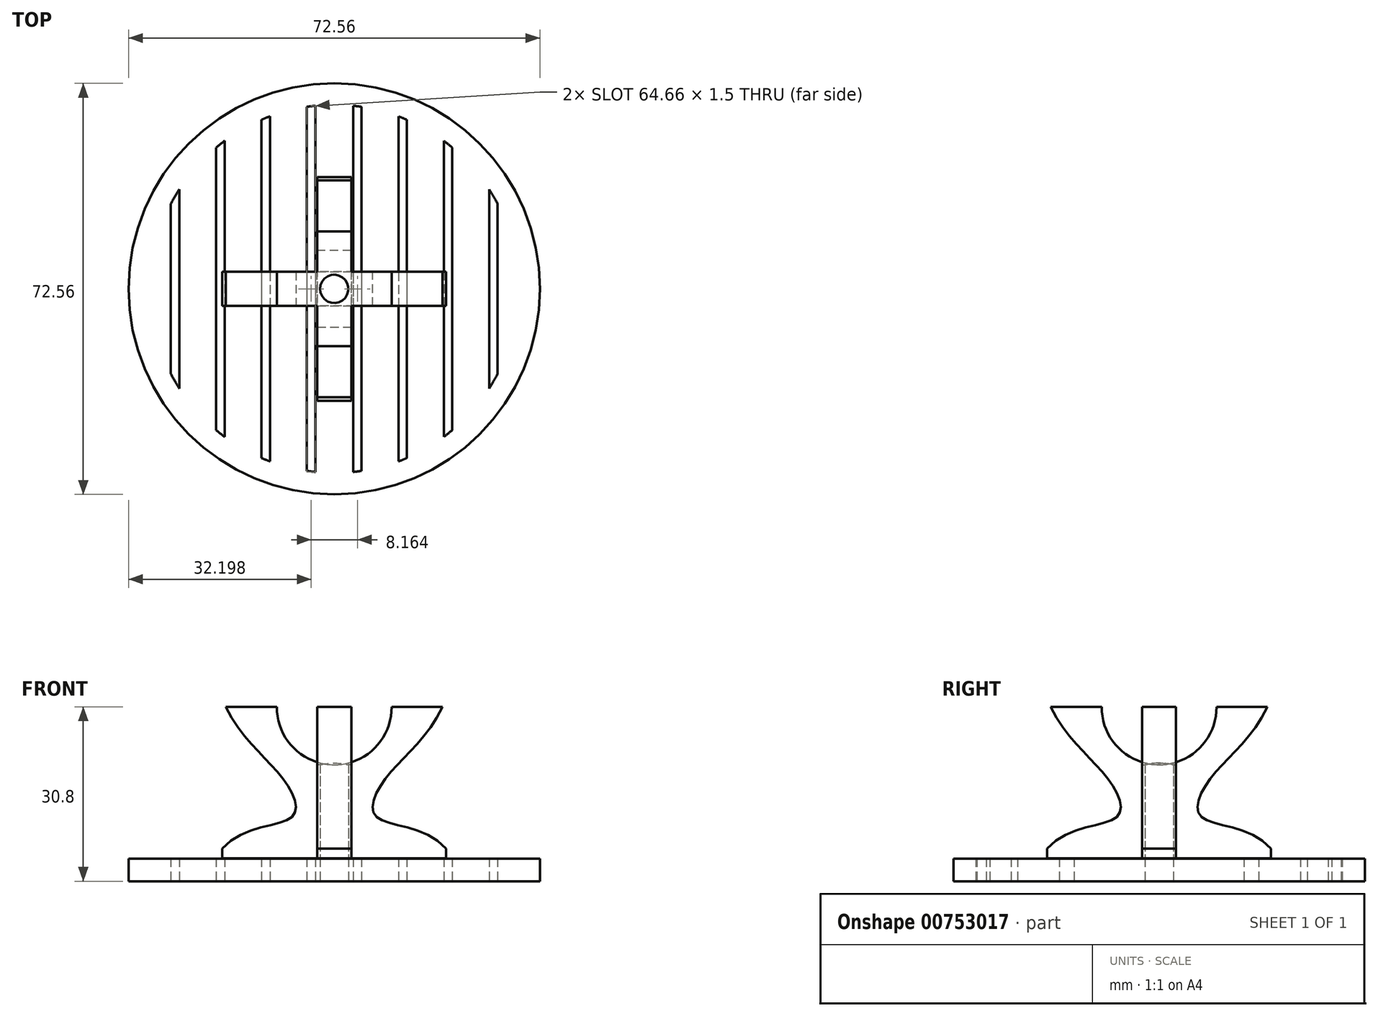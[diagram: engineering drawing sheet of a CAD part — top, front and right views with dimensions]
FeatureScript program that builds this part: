
annotation { "Feature Type Name" : "Feature", "Feature Type Description" : "" }
export const myFeature = defineFeature(function(context is Context, id is Id, definition is map)
    precondition{}
    {
        {
            var Q0;
            Q0=qCreatedBy(makeId("Top.planeOp"),FACE);
            var sketch = newSketch(context, id + "F0", { "sketchPlane" : qUnion([Q0])});
            skArc(sketch, "E0", {"start": v(0, -32.5) * mm, "mid": v(1.67, -32.46) * mm, "end": v(3.33, -32.33) * mm});
            skLineSegment(sketch, "E1.right", {"start": v(3.33, 32.33) * mm, "end": v(3.33, -32.33) * mm});
            skPoint(sketch, "E2", {"position": v(0.08, 37.94) * mm});
            skLineSegment(sketch, "E3.1.0.0", {"start": v(4.83, 32.14) * mm, "end": v(4.83, -32.14) * mm});
            skLineSegment(sketch, "E3.1.0.1", {"start": v(11.33, 30.46) * mm, "end": v(11.33, -30.46) * mm});
            skPoint(sketch, "E3.1.0.2", {"position": v(8.08, 37.94) * mm});
            skLineSegment(sketch, "E3.2.0.0", {"start": v(12.83, 29.86) * mm, "end": v(12.83, -29.86) * mm});
            skLineSegment(sketch, "E3.2.0.1", {"start": v(19.33, 26.13) * mm, "end": v(19.33, -26.13) * mm});
            skPoint(sketch, "E3.2.0.2", {"position": v(16.08, 37.94) * mm});
            skLineSegment(sketch, "E3.3.0.0", {"start": v(20.83, 24.95) * mm, "end": v(20.83, -24.95) * mm});
            skLineSegment(sketch, "E3.3.0.1", {"start": v(27.33, 17.58) * mm, "end": v(27.33, -17.58) * mm});
            skPoint(sketch, "E3.3.0.2", {"position": v(24.08, 37.94) * mm});
            skLineSegment(sketch, "E3.4.0.0", {"start": v(28.83, 15) * mm, "end": v(28.83, -15) * mm});
            skPoint(sketch, "E3.4.0.2", {"position": v(32.08, 37.94) * mm});
            skLineSegment(sketch, "E3.direction1", {"start": v(3.33, -37.94) * mm, "end": v(4.83, -37.94) * mm, "construction": true});
            skPoint(sketch, "E1.left.start.orphan", {"position": v(-3.17, 37.94) * mm});
            skPoint(sketch, "E4.orphan", {"position": v(4.83, 37.94) * mm});
            skPoint(sketch, "E5.orphan", {"position": v(3.33, 37.94) * mm});
            skPoint(sketch, "E6.orphan", {"position": v(11.33, 37.94) * mm});
            skPoint(sketch, "E7.orphan", {"position": v(12.83, 37.94) * mm});
            skPoint(sketch, "E8.orphan", {"position": v(19.33, 37.94) * mm});
            skPoint(sketch, "E9.orphan", {"position": v(20.83, 37.94) * mm});
            skPoint(sketch, "E10.orphan", {"position": v(27.33, 37.94) * mm});
            skPoint(sketch, "E11.orphan", {"position": v(28.83, 37.94) * mm});
            skArc(sketch, "E12.trimOffspring", {"start": v(3.33, 32.33) * mm, "mid": v(1.67, 32.46) * mm, "end": v(0, 32.5) * mm});
            skArc(sketch, "E13.trimOffspring", {"start": v(11.33, 30.46) * mm, "mid": v(8.13, 31.47) * mm, "end": v(4.83, 32.14) * mm});
            skArc(sketch, "E14.trimOffspring", {"start": v(19.33, 26.13) * mm, "mid": v(16.19, 28.18) * mm, "end": v(12.83, 29.86) * mm});
            skArc(sketch, "E15.trimOffspring", {"start": v(27.33, 17.58) * mm, "mid": v(24.36, 21.51) * mm, "end": v(20.83, 24.95) * mm});
            skPoint(sketch, "E16.orphan", {"position": v(11.33, -37.94) * mm});
            skPoint(sketch, "E17.orphan", {"position": v(12.83, -37.94) * mm});
            skPoint(sketch, "E18.orphan", {"position": v(19.33, -37.94) * mm});
            skPoint(sketch, "E19.orphan", {"position": v(20.83, -37.94) * mm});
            skPoint(sketch, "E20.orphan", {"position": v(27.33, -37.94) * mm});
            skPoint(sketch, "E21.orphan", {"position": v(28.83, -37.94) * mm});
            skArc(sketch, "E22.trimOffspring", {"start": v(28.83, -15) * mm, "mid": v(32.5, 0) * mm, "end": v(28.83, 15) * mm});
            skArc(sketch, "E23.trimOffspring", {"start": v(12.83, -29.86) * mm, "mid": v(21, -24.8) * mm, "end": v(27.33, -17.58) * mm});
            skArc(sketch, "E24.trimOffspring", {"start": v(4.83, -32.14) * mm, "mid": v(8.13, -31.47) * mm, "end": v(11.33, -30.46) * mm});
            skLineSegment(sketch, "E25.MirrorCS", {"start": v(-11.33, 30.46) * mm, "end": v(-11.33, -30.46) * mm});
            skLineSegment(sketch, "E26.MirrorCS", {"start": v(-12.83, 29.86) * mm, "end": v(-12.83, -29.86) * mm});
            skLineSegment(sketch, "E27.MirrorCS", {"start": v(-27.33, 17.58) * mm, "end": v(-27.33, -17.58) * mm});
            skLineSegment(sketch, "E28.MirrorCS", {"start": v(-19.33, 26.13) * mm, "end": v(-19.33, -26.13) * mm});
            skArc(sketch, "E29.MirrorCS", {"start": v(-28.83, -15) * mm, "mid": v(-32.5, 0) * mm, "end": v(-28.83, 15) * mm});
            skArc(sketch, "E30.MirrorCS", {"start": v(-19.33, 26.13) * mm, "mid": v(-16.19, 28.18) * mm, "end": v(-12.83, 29.86) * mm});
            skArc(sketch, "E31.MirrorCS", {"start": v(0, -32.5) * mm, "mid": v(-1.67, -32.46) * mm, "end": v(-3.33, -32.33) * mm});
            skLineSegment(sketch, "E32.MirrorCS", {"start": v(-20.83, 24.95) * mm, "end": v(-20.83, -24.95) * mm});
            skArc(sketch, "E33.MirrorCS", {"start": v(-12.83, -29.86) * mm, "mid": v(-21, -24.8) * mm, "end": v(-27.33, -17.58) * mm});
            skLineSegment(sketch, "E34.MirrorCS", {"start": v(-28.83, 15) * mm, "end": v(-28.83, -15) * mm});
            skArc(sketch, "E35.MirrorCS", {"start": v(-3.33, 32.33) * mm, "mid": v(-1.67, 32.46) * mm, "end": v(0, 32.5) * mm});
            skArc(sketch, "E36.MirrorCS", {"start": v(-11.33, 30.46) * mm, "mid": v(-8.13, 31.47) * mm, "end": v(-4.83, 32.14) * mm});
            skArc(sketch, "E37.MirrorCS", {"start": v(-27.33, 17.58) * mm, "mid": v(-24.36, 21.51) * mm, "end": v(-20.83, 24.95) * mm});
            skArc(sketch, "E38.MirrorCS", {"start": v(-4.83, -32.14) * mm, "mid": v(-8.13, -31.47) * mm, "end": v(-11.33, -30.46) * mm});
            skLineSegment(sketch, "E39.MirrorCS", {"start": v(-3.33, 32.33) * mm, "end": v(-3.33, -32.33) * mm});
            skLineSegment(sketch, "E40.MirrorCS", {"start": v(-4.83, 32.14) * mm, "end": v(-4.83, -32.14) * mm});
            skCircle(sketch, "E41", {"center": v(0, 0) * mm, "radius": 2.5 * mm});
            skSolve(sketch);
        }
        {
            var Q0;
            Q0 = qSketchRegion(id + "F0", true);
            var Q1;
            Q1 = qSketchRegion(id + "F2", true);
            extrude(context, id + "F1", {"entities" : qUnion([Q0, Q1]), "depth" : 4 * mm, "offsetDistance" : 25 * mm});
        }
        {
            var Q0;
            Q0=qCreatedBy(makeId("Top.planeOp"),FACE);
            var sketch = newSketch(context, id + "F2", { "sketchPlane" : qUnion([Q0])});
            skCircle(sketch, "E42", {"center": v(0, 0) * mm, "radius": 36.28 * mm});
            skCircle(sketch, "E43", {"center": v(0, 0) * mm, "radius": 32.5 * mm});
            skSolve(sketch);
        }
        {
            var Q0;
            Q0=makeQuery(id+"F2.imprint","IMPRINT",FACE,{"disambiguationData":[TD([[makeQuery(id+"F2.imprint","IMPRINT",EDGE,{"derivedFrom":sQuery(id+"F2.wireOp",EDGE,"E42")}),1.0]])]});
            extrude(context, id + "F3", {"entities" : qUnion([Q0]), "depth" : 4 * mm, "offsetDistance" : 25 * mm});
        }
        {
            var Q0;
            Q0=makeQuery(id+"F1.opExtrude","SWEPT_BODY",BODY,{"disambiguationData":[OSD([sQuery(id+"F0.wireOp",EDGE,"E0"),sQuery(id+"F0.wireOp",EDGE,"E1.right"),sQuery(id+"F0.wireOp",EDGE,"E12.trimOffspring"),sQuery(id+"F0.wireOp",EDGE,"E31.MirrorCS"),sQuery(id+"F0.wireOp",EDGE,"E35.MirrorCS"),sQuery(id+"F0.wireOp",EDGE,"E39.MirrorCS"),sQuery(id+"F0.wireOp",EDGE,"E41")])]});
            var Q1;
            Q1=makeQuery(id+"F1.opExtrude","SWEPT_BODY",BODY,{"disambiguationData":[OSD([sQuery(id+"F0.wireOp",EDGE,"E3.1.0.0"),sQuery(id+"F0.wireOp",EDGE,"E3.1.0.1"),sQuery(id+"F0.wireOp",EDGE,"E13.trimOffspring"),sQuery(id+"F0.wireOp",EDGE,"E24.trimOffspring")])]});
            var Q2;
            Q2=makeQuery(id+"F1.opExtrude","SWEPT_BODY",BODY,{"disambiguationData":[OSD([sQuery(id+"F0.wireOp",EDGE,"E3.2.0.0"),sQuery(id+"F0.wireOp",EDGE,"E3.2.0.1"),sQuery(id+"F0.wireOp",EDGE,"E14.trimOffspring"),sQuery(id+"F0.wireOp",EDGE,"E23.trimOffspring")])]});
            var Q3;
            Q3=makeQuery(id+"F1.opExtrude","SWEPT_BODY",BODY,{"disambiguationData":[OSD([sQuery(id+"F0.wireOp",EDGE,"E3.3.0.0"),sQuery(id+"F0.wireOp",EDGE,"E3.3.0.1"),sQuery(id+"F0.wireOp",EDGE,"E15.trimOffspring"),sQuery(id+"F0.wireOp",EDGE,"E23.trimOffspring")])]});
            var Q4;
            Q4=makeQuery(id+"F1.opExtrude","SWEPT_BODY",BODY,{"disambiguationData":[OSD([sQuery(id+"F0.wireOp",EDGE,"E3.4.0.0"),sQuery(id+"F0.wireOp",EDGE,"E22.trimOffspring")])]});
            var Q5;
            Q5=makeQuery(id+"F1.opExtrude","SWEPT_BODY",BODY,{"disambiguationData":[OSD([sQuery(id+"F0.wireOp",EDGE,"E25.MirrorCS"),sQuery(id+"F0.wireOp",EDGE,"E36.MirrorCS"),sQuery(id+"F0.wireOp",EDGE,"E38.MirrorCS"),sQuery(id+"F0.wireOp",EDGE,"E40.MirrorCS")])]});
            var Q6;
            Q6=makeQuery(id+"F1.opExtrude","SWEPT_BODY",BODY,{"disambiguationData":[OSD([sQuery(id+"F0.wireOp",EDGE,"E26.MirrorCS"),sQuery(id+"F0.wireOp",EDGE,"E28.MirrorCS"),sQuery(id+"F0.wireOp",EDGE,"E30.MirrorCS"),sQuery(id+"F0.wireOp",EDGE,"E33.MirrorCS")])]});
            var Q7;
            Q7=makeQuery(id+"F1.opExtrude","SWEPT_BODY",BODY,{"disambiguationData":[OSD([sQuery(id+"F0.wireOp",EDGE,"E27.MirrorCS"),sQuery(id+"F0.wireOp",EDGE,"E32.MirrorCS"),sQuery(id+"F0.wireOp",EDGE,"E33.MirrorCS"),sQuery(id+"F0.wireOp",EDGE,"E37.MirrorCS")])]});
            var Q8;
            Q8=makeQuery(id+"F1.opExtrude","SWEPT_BODY",BODY,{"disambiguationData":[OSD([sQuery(id+"F0.wireOp",EDGE,"E29.MirrorCS"),sQuery(id+"F0.wireOp",EDGE,"E34.MirrorCS")])]});
            var Q9;
            Q9=makeQuery(id+"F3.opExtrude","SWEPT_BODY",BODY,{"disambiguationData":[OSD([sQuery(id+"F2.wireOp",EDGE,"E42"),sQuery(id+"F2.wireOp",EDGE,"E43")])]});
            booleanBodies(context, id + "F4", {"operationType" : BooleanOperationType.UNION, "tools" : qUnion([Q0, Q1, Q2, Q3, Q4, Q5, Q6, Q7, Q8, Q9])});
        }
        {
            var Q0;
            Q0=qCreatedBy(makeId("Right.planeOp"),FACE);
            var sketch = newSketch(context, id + "F5", { "sketchPlane" : qUnion([Q0])});
            skFitSpline(sketch, "E44", {"points": [v(19.74, 5.75) * mm, v(7.29, 11.52) * mm, v(9.1, 18.2) * mm, v(19.13, 30.8) * mm], "startDerivative": vector(-32.17, 37.18) * mm, "endDerivative": vector(22.8, 46.74) * mm});
            skFitSpline(sketch, "E45.MirrorCS", {"points": [v(-19.74, 5.75) * mm, v(-7.29, 11.52) * mm, v(-9.1, 18.2) * mm, v(-19.13, 30.8) * mm], "startDerivative": vector(32.17, 37.18) * mm, "endDerivative": vector(-22.8, 46.74) * mm});
            skLineSegment(sketch, "E46", {"start": v(19.13, 30.8) * mm, "end": v(10.12, 30.8) * mm});
            skLineSegment(sketch, "E47", {"start": v(19.74, 5.75) * mm, "end": v(19.74, 4.04) * mm});
            skLineSegment(sketch, "E48", {"start": v(19.74, 4.04) * mm, "end": v(-19.74, 4.04) * mm});
            skLineSegment(sketch, "E49", {"start": v(-19.74, 4.04) * mm, "end": v(-19.74, 5.75) * mm});
            skArc(sketch, "E50", {"start": v(-10.12, 30.8) * mm, "mid": v(0, 20.55) * mm, "end": v(10.12, 30.8) * mm});
            skLineSegment(sketch, "E51.trimOffspring", {"start": v(-10.12, 30.8) * mm, "end": v(-19.13, 30.8) * mm});
            skSolve(sketch);
        }
        {
            var Q0;
            Q0=qCreatedBy(makeId("Right.planeOp"),FACE);
            var sketch = newSketch(context, id + "F6", { "sketchPlane" : qUnion([Q0])});
            skLineSegment(sketch, "E52", {"start": v(0, 0) * mm, "end": v(0, -32.7) * mm, "construction": true});
            skSolve(sketch);
        }
        {
            var Q0;
            Q0=makeQuery(id+"F5.imprint","IMPRINT",FACE,{"disambiguationData":[TD([[makeQuery(id+"F5.imprint","IMPRINT",EDGE,{"derivedFrom":sQuery(id+"F5.wireOp",EDGE,"E44")}),1.0]])]});
            extrude(context, id + "F7", {"entities" : qUnion([Q0]), "endBound" : BoundingType.SYMMETRIC, "depth" : 6 * mm, "offsetDistance" : 25 * mm});
        }
        {
            var Q0;
            Q0=makeQuery(id+"F7.opExtrude","SWEPT_BODY",BODY,{"disambiguationData":[OSD([sQuery(id+"F5.wireOp",EDGE,"E44"),sQuery(id+"F5.wireOp",EDGE,"E45.MirrorCS"),sQuery(id+"F5.wireOp",EDGE,"E46"),sQuery(id+"F5.wireOp",EDGE,"E47"),sQuery(id+"F5.wireOp",EDGE,"E48"),sQuery(id+"F5.wireOp",EDGE,"E49"),sQuery(id+"F5.wireOp",EDGE,"E50"),sQuery(id+"F5.wireOp",EDGE,"E51.trimOffspring")])]});
            var Q1;
            Q1=sQuery(id+"F6.wireOp",EDGE,"E52");
            var Q2;
            Q2=sQuery(id+"F6.wireOp",EDGE,"E52");
            transform(context, id + "F8", {"entities" : qUnion([Q0]), "transformType" : TransformType.ROTATION, "transformAxis" : qUnion([Q2]), "angle" : 90 * degree, "makeCopy" : true});
        }
        {
            var Q0;
            {var subQ0=sQuery(id+"F0.wireOp",EDGE,"E33.MirrorCS");var subQ1=sQuery(id+"F0.wireOp",EDGE,"E23.trimOffspring");Q0=makeQuery(id+"F4.opBoolean","MERGE",FACE,{"derivedFrom":[makeQuery(id+"F1.opExtrude","CAP_FACE",FACE,{"disambiguationData":[OSD([sQuery(id+"F0.wireOp",EDGE,"E0"),sQuery(id+"F0.wireOp",EDGE,"E1.right"),sQuery(id+"F0.wireOp",EDGE,"E12.trimOffspring"),sQuery(id+"F0.wireOp",EDGE,"E31.MirrorCS"),sQuery(id+"F0.wireOp",EDGE,"E35.MirrorCS"),sQuery(id+"F0.wireOp",EDGE,"E39.MirrorCS"),sQuery(id+"F0.wireOp",EDGE,"E41")])],"isStart":true}),makeQuery(id+"F1.opExtrude","CAP_FACE",FACE,{"disambiguationData":[OSD([sQuery(id+"F0.wireOp",EDGE,"E3.1.0.0"),sQuery(id+"F0.wireOp",EDGE,"E3.1.0.1"),sQuery(id+"F0.wireOp",EDGE,"E13.trimOffspring"),sQuery(id+"F0.wireOp",EDGE,"E24.trimOffspring")])],"isStart":true}),makeQuery(id+"F1.opExtrude","CAP_FACE",FACE,{"disambiguationData":[OSD([sQuery(id+"F0.wireOp",EDGE,"E3.2.0.0"),sQuery(id+"F0.wireOp",EDGE,"E3.2.0.1"),sQuery(id+"F0.wireOp",EDGE,"E14.trimOffspring"),subQ1])],"isStart":true}),makeQuery(id+"F1.opExtrude","CAP_FACE",FACE,{"disambiguationData":[OSD([sQuery(id+"F0.wireOp",EDGE,"E3.3.0.0"),sQuery(id+"F0.wireOp",EDGE,"E3.3.0.1"),sQuery(id+"F0.wireOp",EDGE,"E15.trimOffspring"),subQ1])],"isStart":true}),makeQuery(id+"F1.opExtrude","CAP_FACE",FACE,{"disambiguationData":[OSD([sQuery(id+"F0.wireOp",EDGE,"E3.4.0.0"),sQuery(id+"F0.wireOp",EDGE,"E22.trimOffspring")])],"isStart":true}),makeQuery(id+"F1.opExtrude","CAP_FACE",FACE,{"disambiguationData":[OSD([sQuery(id+"F0.wireOp",EDGE,"E25.MirrorCS"),sQuery(id+"F0.wireOp",EDGE,"E36.MirrorCS"),sQuery(id+"F0.wireOp",EDGE,"E38.MirrorCS"),sQuery(id+"F0.wireOp",EDGE,"E40.MirrorCS")])],"isStart":true}),makeQuery(id+"F1.opExtrude","CAP_FACE",FACE,{"disambiguationData":[OSD([sQuery(id+"F0.wireOp",EDGE,"E26.MirrorCS"),sQuery(id+"F0.wireOp",EDGE,"E28.MirrorCS"),sQuery(id+"F0.wireOp",EDGE,"E30.MirrorCS"),subQ0])],"isStart":true}),makeQuery(id+"F1.opExtrude","CAP_FACE",FACE,{"disambiguationData":[OSD([sQuery(id+"F0.wireOp",EDGE,"E27.MirrorCS"),sQuery(id+"F0.wireOp",EDGE,"E32.MirrorCS"),subQ0,sQuery(id+"F0.wireOp",EDGE,"E37.MirrorCS")])],"isStart":true}),makeQuery(id+"F1.opExtrude","CAP_FACE",FACE,{"disambiguationData":[OSD([sQuery(id+"F0.wireOp",EDGE,"E29.MirrorCS"),sQuery(id+"F0.wireOp",EDGE,"E34.MirrorCS")])],"isStart":true}),makeQuery(id+"F3.opExtrude","CAP_FACE",FACE,{"disambiguationData":[OSD([sQuery(id+"F2.wireOp",EDGE,"E42"),sQuery(id+"F2.wireOp",EDGE,"E43")])],"isStart":true})]});}
            var sketch = newSketch(context, id + "F9", { "sketchPlane" : qUnion([Q0])});
            skCircle(sketch, "E53", {"center": v(0, 0) * mm, "radius": 2.5 * mm});
            skSolve(sketch);
        }
        {
            var Q0;
            Q0=makeQuery(id+"F9.imprint","IMPRINT",FACE,{"disambiguationData":[TD([[makeQuery(id+"F9.imprint","IMPRINT",EDGE,{"derivedFrom":sQuery(id+"F9.wireOp",EDGE,"E53")}),-1.0]])]});
            extrude(context, id + "F10", {"entities" : qUnion([Q0]), "operationType" : NewBodyOperationType.REMOVE, "endBound" : BoundingType.THROUGH_ALL, "oppositeDirection" : true, "depth" : 25 * mm, "offsetDistance" : 25 * mm});
        }
    });
